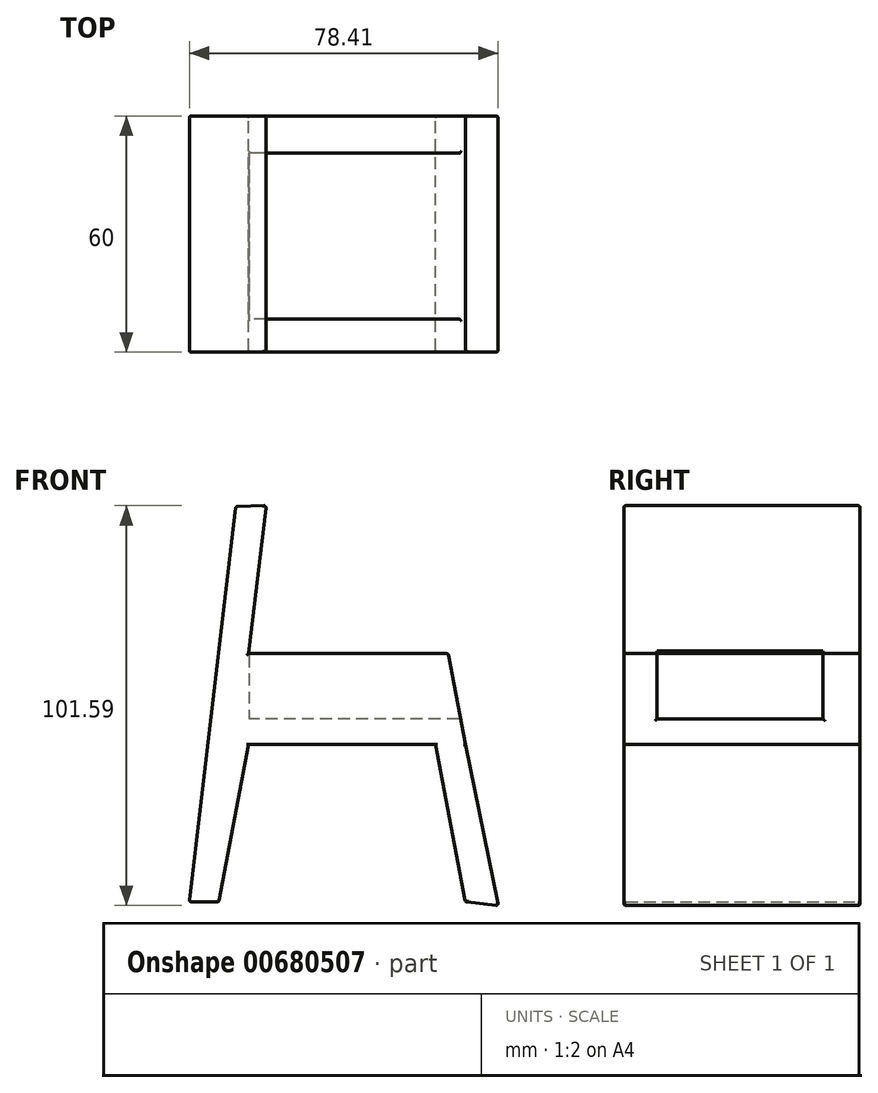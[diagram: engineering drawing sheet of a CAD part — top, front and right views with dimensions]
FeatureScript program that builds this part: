
annotation { "Feature Type Name" : "Feature", "Feature Type Description" : "" }
export const myFeature = defineFeature(function(context is Context, id is Id, definition is map)
    precondition{}
    {
        {
            var Q0;
            Q0=qCreatedBy(makeId("Front.planeOp"),FACE);
            var sketch = newSketch(context, id + "F0", { "sketchPlane" : qUnion([Q0])});
            skLineSegment(sketch, "E0", {"start": v(-34.3, 45.36) * mm, "end": v(-46.17, -55.08) * mm});
            skLineSegment(sketch, "E1", {"start": v(-46.17, -55.08) * mm, "end": v(-38.61, -55.08) * mm});
            skLineSegment(sketch, "E2", {"start": v(-38.61, -55.08) * mm, "end": v(-31.05, -15.12) * mm});
            skLineSegment(sketch, "E3", {"start": v(-31.05, -15.12) * mm, "end": v(16.47, -15.12) * mm});
            skLineSegment(sketch, "E4", {"start": v(16.47, -15.12) * mm, "end": v(24.03, -55.08) * mm});
            skLineSegment(sketch, "E5", {"start": v(24.03, -55.08) * mm, "end": v(32.43, -56.08) * mm});
            skLineSegment(sketch, "E6", {"start": v(32.43, -56.08) * mm, "end": v(24.03, -15.12) * mm});
            skLineSegment(sketch, "E7", {"start": v(24.03, -15.12) * mm, "end": v(19.65, 8.02) * mm});
            skLineSegment(sketch, "E8", {"start": v(19.65, 8.02) * mm, "end": v(-31.05, 8.02) * mm});
            skLineSegment(sketch, "E9", {"start": v(-31.05, 8.02) * mm, "end": v(-26.6, 45.6) * mm});
            skLineSegment(sketch, "E10", {"start": v(-26.6, 45.6) * mm, "end": v(-34.3, 45.36) * mm});
            skSolve(sketch);
        }
        {
            var Q0;
            Q0=makeQuery(id+"F0.imprint","IMPRINT",FACE,{"disambiguationData":[TD([[makeQuery(id+"F0.imprint","IMPRINT",EDGE,{"derivedFrom":sQuery(id+"F0.wireOp",EDGE,"E0")}),1.0]])]});
            extrude(context, id + "F1", {"entities" : qUnion([Q0]), "depth" : 60 * mm, "offsetDistance" : 25.4 * mm});
        }
        {
            var Q0;
            Q0=qCreatedBy(makeId("Right.planeOp"),FACE);
            var sketch = newSketch(context, id + "F2", { "sketchPlane" : qUnion([Q0])});
            skLineSegment(sketch, "E11", {"start": v(-51.57, 8.64) * mm, "end": v(-51.57, -8.64) * mm});
            skLineSegment(sketch, "E12", {"start": v(-51.57, -8.64) * mm, "end": v(-9.45, -8.64) * mm});
            skLineSegment(sketch, "E13", {"start": v(-9.45, -8.64) * mm, "end": v(-9.45, 8.64) * mm});
            skLineSegment(sketch, "E14", {"start": v(-9.45, 8.64) * mm, "end": v(-51.57, 8.64) * mm});
            skSolve(sketch);
        }
        {
            var Q0;
            Q0 = qSketchRegion(id + "F2", true);
            extrude(context, id + "F3", {"entities" : qUnion([Q0]), "operationType" : NewBodyOperationType.REMOVE, "depth" : 35 * mm, "offsetDistance" : 25 * mm, "hasSecondDirection" : true, "secondDirectionOppositeDirection" : true, "secondDirectionDepth" : 31 * mm});
        }
        {
            var Q0;
            Q0=makeQuery(id+"F1.opExtrude","CAP_EDGE",EDGE,{"disambiguationData":[OSD([sQuery(id+"F0.wireOp",EDGE,"E10")])],"isStart":true});
            fillet(context, id + "F4", {"entities" : qUnion([Q0]), "radius" : 0.5 * mm, "tangentPropagation" : true, "allowEdgeOverflow" : false});
        }
        {
            var Q0;
            Q0=makeQuery(id+"F1.opExtrude","CAP_EDGE",EDGE,{"disambiguationData":[OSD([sQuery(id+"F0.wireOp",EDGE,"E10")])],"isStart":false});
            var Q1;
            Q1=makeQuery(id+"F1.opExtrude","CAP_EDGE",EDGE,{"disambiguationData":[OSD([sQuery(id+"F0.wireOp",EDGE,"E9")])],"isStart":false});
            fillet(context, id + "F5", {"entities" : qUnion([Q0, Q1]), "radius" : .5 * mm, "tangentPropagation" : true, "allowEdgeOverflow" : false});
        }
        {
            var Q0;
            Q0=makeQuery(id+"F1.opExtrude","CAP_EDGE",EDGE,{"disambiguationData":[OSD([sQuery(id+"F0.wireOp",EDGE,"E0")])],"isStart":false});
            fillet(context, id + "F6", {"entities" : qUnion([Q0]), "radius" : .5 * mm, "tangentPropagation" : true, "allowEdgeOverflow" : false});
        }
        {
            var Q0;
            Q0=makeQuery(id+"F1.opExtrude","CAP_EDGE",EDGE,{"disambiguationData":[OSD([sQuery(id+"F0.wireOp",EDGE,"E8")])],"isStart":false});
            fillet(context, id + "F7", {"entities" : qUnion([Q0]), "radius" : .5 * mm, "tangentPropagation" : true, "allowEdgeOverflow" : false});
        }
        {
            var Q0;
            {var subQ0=sQuery(id+"F0.wireOp",EDGE,"E8");var subQ1=sQuery(id+"F0.wireOp",EDGE,"E7");Q0=makeQuery(id+"F3.boolean.opBoolean","SPLIT",EDGE,{"disambiguationData":[TD([makeQuery(id+"F3.opExtrude","SWEPT_FACE",FACE,{"disambiguationData":[OSD([sQuery(id+"F2.wireOp",EDGE,"E11")])]})])],"derivedFrom":makeQuery(id+"F1.opExtrude","SWEPT_EDGE",EDGE,{"disambiguationData":[OSD([subQ1,subQ0])]})});}
            fillet(context, id + "F8", {"entities" : qUnion([Q0]), "radius" : .5 * mm, "tangentPropagation" : true, "allowEdgeOverflow" : false});
        }
        {
            var Q0;
            Q0=makeQuery(id+"F3.boolean.opBoolean","INTERSECT",EDGE,{"derivedFrom":[makeQuery(id+"F1.opExtrude","SWEPT_FACE",FACE,{"disambiguationData":[OSD([sQuery(id+"F0.wireOp",EDGE,"E8")])]}),makeQuery(id+"F3.opExtrude","SWEPT_FACE",FACE,{"disambiguationData":[OSD([sQuery(id+"F2.wireOp",EDGE,"E11")])]})]});
            fillet(context, id + "F9", {"entities" : qUnion([Q0]), "radius" : .5 * mm, "tangentPropagation" : true, "allowEdgeOverflow" : false});
        }
        {
            var Q0;
            Q0=makeQuery(id+"F3.boolean.opBoolean","INTERSECT",EDGE,{"derivedFrom":[makeQuery(id+"F1.opExtrude","SWEPT_FACE",FACE,{"disambiguationData":[OSD([sQuery(id+"F0.wireOp",EDGE,"E8")])]}),makeQuery(id+"F3.opExtrude","SWEPT_FACE",FACE,{"disambiguationData":[OSD([sQuery(id+"F2.wireOp",EDGE,"E13")])]})]});
            fillet(context, id + "F10", {"entities" : qUnion([Q0]), "radius" : .5 * mm, "tangentPropagation" : true, "allowEdgeOverflow" : false});
        }
        {
            var Q0;
            {var subQ0=sQuery(id+"F0.wireOp",EDGE,"E8");var subQ1=sQuery(id+"F0.wireOp",EDGE,"E7");Q0=makeQuery(id+"F3.boolean.opBoolean","SPLIT",EDGE,{"disambiguationData":[TD([makeQuery(id+"F3.opExtrude","SWEPT_FACE",FACE,{"disambiguationData":[OSD([sQuery(id+"F2.wireOp",EDGE,"E13")])]})])],"derivedFrom":makeQuery(id+"F1.opExtrude","SWEPT_EDGE",EDGE,{"disambiguationData":[OSD([subQ1,subQ0])]})});}
            fillet(context, id + "F11", {"entities" : qUnion([Q0]), "radius" : .5 * mm, "tangentPropagation" : true, "allowEdgeOverflow" : false});
        }
        {
            var Q0;
            Q0=makeQuery(id+"F1.opExtrude","CAP_EDGE",EDGE,{"disambiguationData":[OSD([sQuery(id+"F0.wireOp",EDGE,"E8")])],"isStart":true});
            fillet(context, id + "F12", {"entities" : qUnion([Q0]), "radius" : .5 * mm, "tangentPropagation" : true, "allowEdgeOverflow" : false});
        }
        {
            var Q0;
            Q0=makeQuery(id+"F3.boolean.opBoolean","INTERSECT",EDGE,{"derivedFrom":[makeQuery(id+"F1.opExtrude","SWEPT_FACE",FACE,{"disambiguationData":[OSD([sQuery(id+"F0.wireOp",EDGE,"E7")])]}),makeQuery(id+"F3.opExtrude","SWEPT_FACE",FACE,{"disambiguationData":[OSD([sQuery(id+"F2.wireOp",EDGE,"E12")])]})]});
            fillet(context, id + "F13", {"entities" : qUnion([Q0]), "radius" : .5 * mm, "tangentPropagation" : true, "allowEdgeOverflow" : false});
        }
        {
            var Q0;
            Q0=makeQuery(id+"F1.opExtrude","SWEPT_EDGE",EDGE,{"disambiguationData":[OSD([sQuery(id+"F0.wireOp",EDGE,"E5"),sQuery(id+"F0.wireOp",EDGE,"E6")])]});
            fillet(context, id + "F14", {"entities" : qUnion([Q0]), "radius" : .5 * mm, "tangentPropagation" : true, "allowEdgeOverflow" : false});
        }
        {
            var Q0;
            Q0=makeQuery(id+"F1.opExtrude","SWEPT_EDGE",EDGE,{"disambiguationData":[OSD([sQuery(id+"F0.wireOp",EDGE,"E9"),sQuery(id+"F0.wireOp",EDGE,"E10")])]});
            fillet(context, id + "F15", {"entities" : qUnion([Q0]), "radius" : .5 * mm, "tangentPropagation" : true, "allowEdgeOverflow" : false});
        }
        {
            var Q0;
            Q0=makeQuery(id+"F1.opExtrude","SWEPT_FACE",FACE,{"disambiguationData":[OSD([sQuery(id+"F0.wireOp",EDGE,"E1")])]});
            fillet(context, id + "F16", {"entities" : qUnion([Q0]), "radius" : .5 * mm, "tangentPropagation" : true, "allowEdgeOverflow" : false});
        }
        {
            var Q0;
            Q0=makeQuery(id+"F1.opExtrude","SWEPT_EDGE",EDGE,{"disambiguationData":[OSD([sQuery(id+"F0.wireOp",EDGE,"E4"),sQuery(id+"F0.wireOp",EDGE,"E5")])]});
            fillet(context, id + "F17", {"entities" : qUnion([Q0]), "radius" : .5 * mm, "tangentPropagation" : true, "allowEdgeOverflow" : false});
        }
        {
            var Q0;
            Q0=makeQuery(id+"F1.opExtrude","CAP_EDGE",EDGE,{"disambiguationData":[OSD([sQuery(id+"F0.wireOp",EDGE,"E2")])],"isStart":false});
            fillet(context, id + "F18", {"entities" : qUnion([Q0]), "radius" : .5 * mm, "tangentPropagation" : true, "allowEdgeOverflow" : false});
        }
        {
            var Q0;
            Q0=makeQuery(id+"F1.opExtrude","CAP_EDGE",EDGE,{"disambiguationData":[OSD([sQuery(id+"F0.wireOp",EDGE,"E2")])],"isStart":true});
            fillet(context, id + "F19", {"entities" : qUnion([Q0]), "radius" : .5 * mm, "tangentPropagation" : true, "allowEdgeOverflow" : false});
        }
    });
